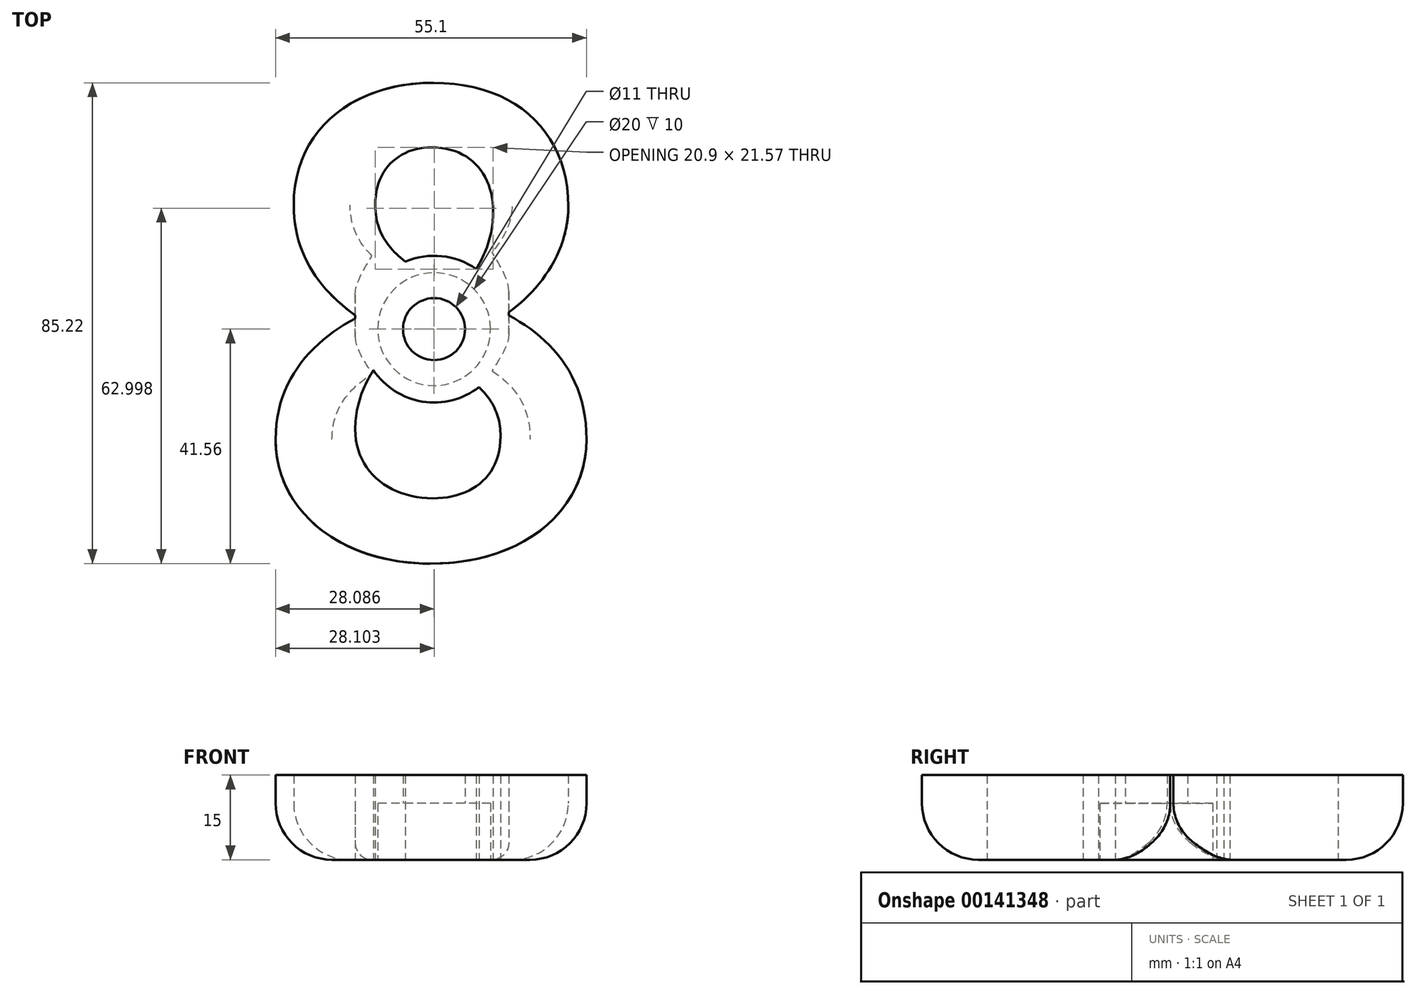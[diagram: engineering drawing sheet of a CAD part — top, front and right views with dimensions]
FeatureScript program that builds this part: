
annotation { "Feature Type Name" : "Feature", "Feature Type Description" : "" }
export const myFeature = defineFeature(function(context is Context, id is Id, definition is map)
    precondition{}
    {
        {
            var Q0;
            Q0=qCreatedBy(makeId("Top.planeOp"),FACE);
            var sketch = newSketch(context, id + "F0", { "sketchPlane" : qUnion([Q0])});
            skText(sketch, "E0", { "text": "8", "fontName": "NotoSansCJKsc-Bold.otf"});
            skCircle(sketch, "E1", {"center": v(33.32, -40) * mm, "radius": 13 * mm});
            skCircle(sketch, "E2", {"center": v(33.32, -40) * mm, "radius": 10 * mm});
            skCircle(sketch, "E3", {"center": v(33.32, -40) * mm, "radius": 5.5 * mm});
            const initialGuessF0  = {"E0": [0, -0.08, 1, 0, 0.08]};
            skSetInitialGuess(sketch, initialGuessF0);
            skSolve(sketch);
        }
        {
            var Q0;
            Q0=makeQuery(id+"F0.imprint","IMPRINT",FACE,{"disambiguationData":[TD([[makeQuery(id+"F0.imprint","IMPRINT",EDGE,{"derivedFrom":sQuery(id+"F0.wireOp",EDGE,"E0.sketch_text.stroke-0")}),1.0]])]});
            var Q1;
            {var subQ0=sQuery(id+"F0.wireOp",EDGE,"E2");var subQ1=sQuery(id+"F0.wireOp",EDGE,"E0.sketch_text.stroke-10");var subQ2=makeQuery(id+"F0.imprint","INTERSECT",VERTEX,{"derivedFrom":[subQ1,subQ0]});Q1=makeQuery(id+"F0.imprint","IMPRINT",FACE,{"disambiguationData":[TD([[makeQuery(id+"F0.imprint","IMPRINT",EDGE,{"disambiguationData":[TD([[subQ2,-1.0]])],"derivedFrom":subQ1}),-1.0]])]});}
            var Q2;
            {var subQ0=sQuery(id+"F0.wireOp",EDGE,"E1");var subQ1=sQuery(id+"F0.wireOp",EDGE,"E0.sketch_text.stroke-15");var subQ2=makeQuery(id+"F0.imprint","INTERSECT",VERTEX,{"derivedFrom":[subQ1,subQ0]});Q2=makeQuery(id+"F0.imprint","IMPRINT",FACE,{"disambiguationData":[TD([[makeQuery(id+"F0.imprint","IMPRINT",EDGE,{"disambiguationData":[TD([[subQ2,-1.0]])],"derivedFrom":subQ1}),-1.0]])]});}
            var Q3;
            {var subQ0=sQuery(id+"F0.wireOp",EDGE,"E2");var subQ1=sQuery(id+"F0.wireOp",EDGE,"E0.sketch_text.stroke-10");var subQ2=makeQuery(id+"F0.imprint","INTERSECT",VERTEX,{"derivedFrom":[subQ1,subQ0]});Q3=makeQuery(id+"F0.imprint","IMPRINT",FACE,{"disambiguationData":[TD([[makeQuery(id+"F0.imprint","IMPRINT",EDGE,{"disambiguationData":[TD([[subQ2,-1.0]])],"derivedFrom":subQ1}),1.0]])]});}
            var Q4;
            {var subQ0=sQuery(id+"F0.wireOp",EDGE,"E1");var subQ1=sQuery(id+"F0.wireOp",EDGE,"E0.sketch_text.stroke-13");var subQ2=makeQuery(id+"F0.imprint","INTERSECT",VERTEX,{"derivedFrom":[subQ1,subQ0]});Q4=makeQuery(id+"F0.imprint","IMPRINT",FACE,{"disambiguationData":[TD([[makeQuery(id+"F0.imprint","IMPRINT",EDGE,{"disambiguationData":[TD([[subQ2,-1.0]])],"derivedFrom":subQ1}),1.0]])]});}
            var Q5;
            {var subQ0=sQuery(id+"F0.wireOp",EDGE,"E0.sketch_text.stroke-13");var subQ1=sQuery(id+"F0.wireOp",EDGE,"E0.sketch_text.stroke-10");var subQ2=makeQuery(id+"F0.imprint","INTERSECT",VERTEX,{"derivedFrom":[subQ1,subQ0]});Q5=makeQuery(id+"F0.imprint","IMPRINT",FACE,{"disambiguationData":[TD([[makeQuery(id+"F0.imprint","IMPRINT",EDGE,{"disambiguationData":[TD([[subQ2,-1.0]])],"derivedFrom":subQ1}),-1.0]])]});}
            var Q6;
            {var subQ1=sQuery(id+"F0.wireOp",EDGE,"E0.sketch_text.stroke-16");var subQ5=sQuery(id+"F0.wireOp",EDGE,"E0.sketch_text.stroke-15");var subQ7=makeQuery(id+"F0.imprint","INTERSECT",VERTEX,{"derivedFrom":[subQ5,subQ1]});Q6=makeQuery(id+"F0.imprint","IMPRINT",FACE,{"disambiguationData":[TD([[makeQuery(id+"F0.imprint","IMPRINT",EDGE,{"disambiguationData":[TD([[subQ7,1.0]])],"derivedFrom":subQ5}),-1.0]])]});}
            var Q7;
            {var subQ6=sQuery(id+"F0.wireOp",EDGE,"E0.sketch_text.stroke-10");var subQ9=sQuery(id+"F0.wireOp",EDGE,"E0.sketch_text.stroke-13");var subQ10=makeQuery(id+"F0.imprint","INTERSECT",VERTEX,{"derivedFrom":[subQ6,subQ9]});Q7=makeQuery(id+"F0.imprint","IMPRINT",FACE,{"disambiguationData":[TD([[makeQuery(id+"F0.imprint","IMPRINT",EDGE,{"disambiguationData":[TD([[subQ10,-1.0]])],"derivedFrom":subQ6}),1.0]])]});}
            extrude(context, id + "F1", {"entities" : qUnion([Q0, Q1, Q2, Q3, Q4, Q5, Q6, Q7]), "depth" : 15 * mm});
        }
        {
            var Q0;
            {var subQ6=sQuery(id+"F0.wireOp",EDGE,"E0.sketch_text.stroke-10");var subQ9=sQuery(id+"F0.wireOp",EDGE,"E0.sketch_text.stroke-13");var subQ10=makeQuery(id+"F0.imprint","INTERSECT",VERTEX,{"derivedFrom":[subQ6,subQ9]});Q0=makeQuery(id+"F0.imprint","IMPRINT",FACE,{"disambiguationData":[TD([[makeQuery(id+"F0.imprint","IMPRINT",EDGE,{"disambiguationData":[TD([[subQ10,-1.0]])],"derivedFrom":subQ6}),1.0]])]});}
            var Q1;
            {var subQ0=sQuery(id+"F0.wireOp",EDGE,"E0.sketch_text.stroke-13");var subQ1=sQuery(id+"F0.wireOp",EDGE,"E0.sketch_text.stroke-10");var subQ2=makeQuery(id+"F0.imprint","INTERSECT",VERTEX,{"derivedFrom":[subQ1,subQ0]});Q1=makeQuery(id+"F0.imprint","IMPRINT",FACE,{"disambiguationData":[TD([[makeQuery(id+"F0.imprint","IMPRINT",EDGE,{"disambiguationData":[TD([[subQ2,-1.0]])],"derivedFrom":subQ1}),-1.0]])]});}
            var Q2;
            {var subQ1=sQuery(id+"F0.wireOp",EDGE,"E0.sketch_text.stroke-16");var subQ5=sQuery(id+"F0.wireOp",EDGE,"E0.sketch_text.stroke-15");var subQ7=makeQuery(id+"F0.imprint","INTERSECT",VERTEX,{"derivedFrom":[subQ5,subQ1]});Q2=makeQuery(id+"F0.imprint","IMPRINT",FACE,{"disambiguationData":[TD([[makeQuery(id+"F0.imprint","IMPRINT",EDGE,{"disambiguationData":[TD([[subQ7,1.0]])],"derivedFrom":subQ5}),-1.0]])]});}
            extrude(context, id + "F2", {"entities" : qUnion([Q0, Q1, Q2]), "operationType" : NewBodyOperationType.REMOVE, "depth" : 10 * mm});
        }
        {
            var Q0;
            Q0=makeQuery(id+"F1.opExtrude","CAP_EDGE",EDGE,{"disambiguationData":[OSD([sQuery(id+"F0.wireOp",EDGE,"E0.sketch_text.stroke-5")])],"isStart":true});
            var Q1;
            Q1=makeQuery(id+"F1.opExtrude","CAP_EDGE",EDGE,{"disambiguationData":[OSD([sQuery(id+"F0.wireOp",EDGE,"E0.sketch_text.stroke-8")])],"isStart":true});
            fillet(context, id + "F3", {"entities" : qUnion([Q0, Q1]), "radius" : 10 * mm, "tangentPropagation" : true, "allowEdgeOverflow" : false});
        }
        {
            var Q0;
            Q0=makeQuery(id+"F1.opExtrude","CAP_EDGE",EDGE,{"disambiguationData":[OSD([sQuery(id+"F0.wireOp",EDGE,"E0.sketch_text.stroke-7")])],"isStart":true});
            var Q1;
            Q1=makeQuery(id+"F1.opExtrude","CAP_EDGE",EDGE,{"disambiguationData":[OSD([sQuery(id+"F0.wireOp",EDGE,"E0.sketch_text.stroke-2")])],"isStart":true});
            fillet(context, id + "F4", {"entities" : qUnion([Q0, Q1]), "radius" : 3 * mm, "tangentPropagation" : true, "allowEdgeOverflow" : false});
        }
    });
